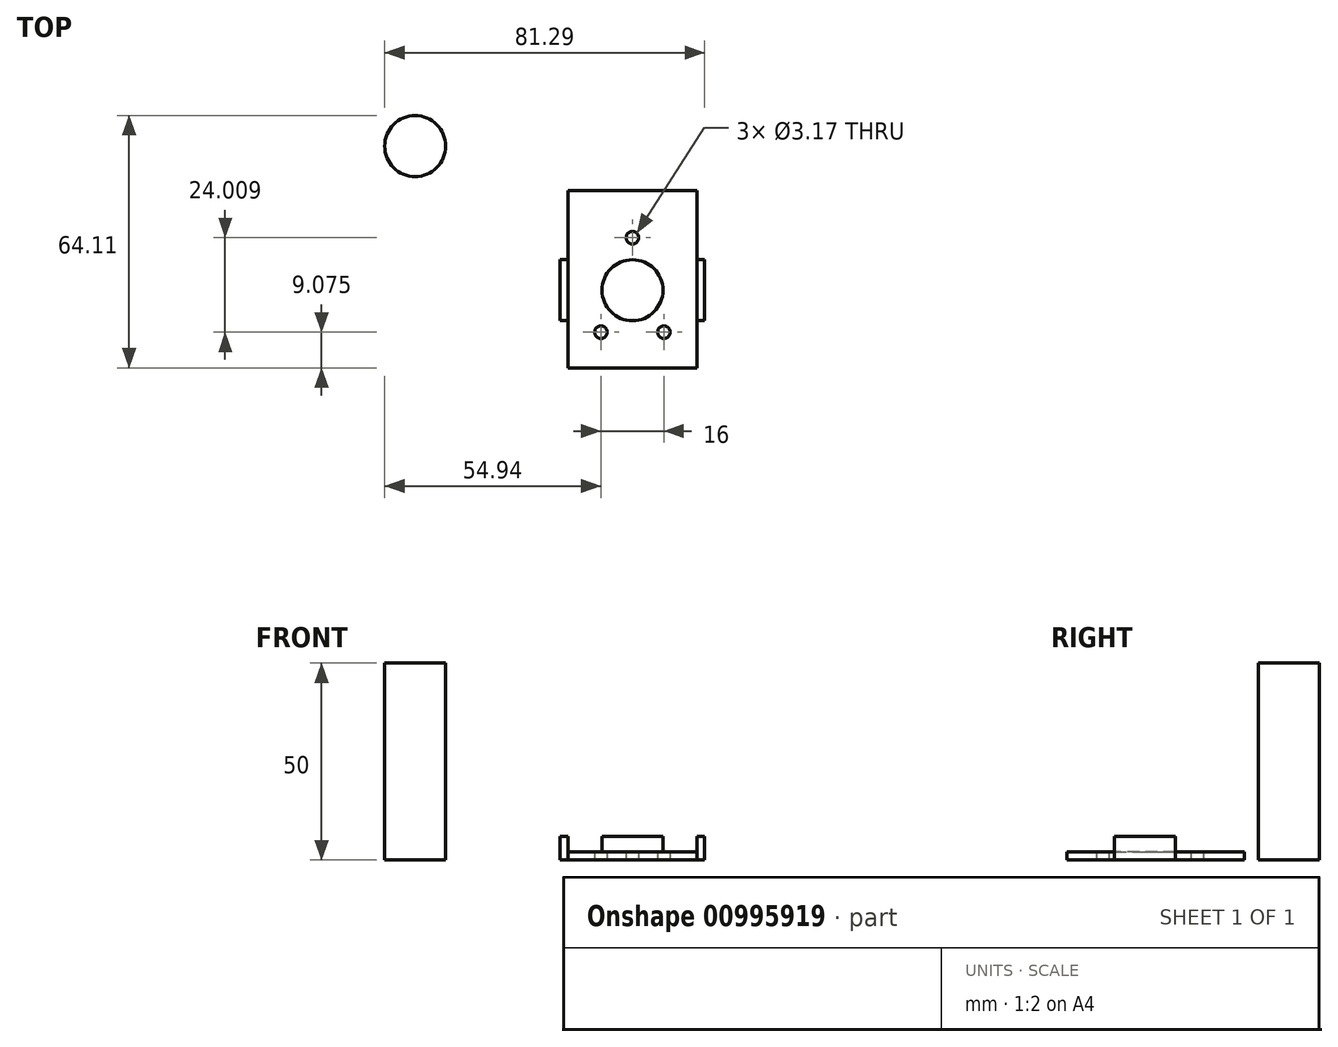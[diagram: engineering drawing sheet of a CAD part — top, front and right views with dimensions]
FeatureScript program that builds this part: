
annotation { "Feature Type Name" : "Feature", "Feature Type Description" : "" }
export const myFeature = defineFeature(function(context is Context, id is Id, definition is map)
    precondition{}
    {
        {
            var Q0;
            Q0=qCreatedBy(makeId("Top.planeOp"),FACE);
            var sketch = newSketch(context, id + "F0", { "sketchPlane" : qUnion([Q0])});
            skCircle(sketch, "E0", {"center": v(0, 0) * mm, "radius": 7.75 * mm});
            skSolve(sketch);
        }
        {
            var Q0;
            Q0 = qSketchRegion(id + "F0", true);
            extrude(context, id + "F1", {"entities" : qUnion([Q0]), "depth" : 50 * mm, "offsetDistance" : 25 * mm});
        }
        {
            var Q0;
            Q0=qCreatedBy(makeId("Top.planeOp"),FACE);
            var sketch = newSketch(context, id + "F2", { "sketchPlane" : qUnion([Q0])});
            skCircle(sketch, "E1", {"center": v(55.2, -36.61) * mm, "radius": 7.75 * mm});
            skLineSegment(sketch, "E2.bottom", {"start": v(38.84, -11.36) * mm, "end": v(71.54, -11.36) * mm});
            skLineSegment(sketch, "E2.top", {"start": v(38.84, -56.36) * mm, "end": v(71.54, -56.36) * mm});
            skLineSegment(sketch, "E2.left", {"start": v(38.84, -11.36) * mm, "end": v(38.84, -56.36) * mm});
            skLineSegment(sketch, "E2.right", {"start": v(71.54, -11.36) * mm, "end": v(71.54, -56.36) * mm});
            skPoint(sketch, "E3", {"position": v(55.2, -56.36) * mm});
            skCircle(sketch, "E4", {"center": v(47.2, -47.28) * mm, "radius": 1.59 * mm});
            skCircle(sketch, "E5", {"center": v(63.2, -47.28) * mm, "radius": 1.59 * mm});
            skCircle(sketch, "E6", {"center": v(55.2, -23.28) * mm, "radius": 1.59 * mm});
            skPoint(sketch, "E6.centerSnap0", {"position": v(55.2, -11.36) * mm});
            skLineSegment(sketch, "E7", {"start": v(47.2, -47.28) * mm, "end": v(55.2, -36.61) * mm, "construction": true});
            skLineSegment(sketch, "E8", {"start": v(63.2, -47.28) * mm, "end": v(55.2, -36.61) * mm, "construction": true});
            skLineSegment(sketch, "E9", {"start": v(55.2, -36.61) * mm, "end": v(55.2, -23.28) * mm, "construction": true});
            skLineSegment(sketch, "E10.bottom", {"start": v(71.54, -28.86) * mm, "end": v(73.54, -28.86) * mm});
            skLineSegment(sketch, "E10.top", {"start": v(71.54, -44.36) * mm, "end": v(73.54, -44.36) * mm});
            skLineSegment(sketch, "E10.left", {"start": v(71.54, -28.86) * mm, "end": v(71.54, -44.36) * mm});
            skLineSegment(sketch, "E10.right", {"start": v(73.54, -28.86) * mm, "end": v(73.54, -44.36) * mm});
            skLineSegment(sketch, "E11.bottom", {"start": v(38.84, -28.86) * mm, "end": v(36.84, -28.86) * mm});
            skLineSegment(sketch, "E11.top", {"start": v(38.84, -44.36) * mm, "end": v(36.84, -44.36) * mm});
            skLineSegment(sketch, "E11.left", {"start": v(38.84, -28.86) * mm, "end": v(38.84, -44.36) * mm});
            skLineSegment(sketch, "E11.right", {"start": v(36.84, -28.86) * mm, "end": v(36.84, -44.36) * mm});
            skSolve(sketch);
        }
        {
            var Q0;
            {var subQ0=sQuery(id+"F2.wireOp",EDGE,"E10.bottom");var subQ6=sQuery(id+"F2.wireOp",EDGE,"E11.bottom");Q0=qUnion([makeQuery(id+"F2.imprint","IMPRINT",FACE,{"disambiguationData":[TD([[makeQuery(id+"F2.imprint","IMPRINT",EDGE,{"derivedFrom":sQuery(id+"F2.wireOp",EDGE,"E1")}),-1.0]])]}),makeQuery(id+"F2.imprint","IMPRINT",FACE,{"disambiguationData":[TD([[makeQuery(id+"F2.imprint","IMPRINT",EDGE,{"derivedFrom":subQ6}),1.0]])]}),makeQuery(id+"F2.imprint","IMPRINT",FACE,{"disambiguationData":[TD([[makeQuery(id+"F2.imprint","IMPRINT",EDGE,{"derivedFrom":subQ0}),-1.0]])]})]);}
            extrude(context, id + "F3", {"entities" : qUnion([Q0]), "depth" : 2 * mm, "offsetDistance" : 25 * mm});
        }
        {
            var Q0;
            Q0=makeQuery(id+"F2.imprint","IMPRINT",FACE,{"disambiguationData":[TD([[makeQuery(id+"F2.imprint","IMPRINT",EDGE,{"derivedFrom":sQuery(id+"F2.wireOp",EDGE,"E1")}),1.0]])]});
            var Q1;
            {var subQ0=sQuery(id+"F2.wireOp",EDGE,"E11.bottom");Q1=makeQuery(id+"F2.imprint","IMPRINT",FACE,{"disambiguationData":[TD([[makeQuery(id+"F2.imprint","IMPRINT",EDGE,{"derivedFrom":subQ0}),1.0]])]});}
            var Q2;
            {var subQ0=sQuery(id+"F2.wireOp",EDGE,"E10.bottom");Q2=makeQuery(id+"F2.imprint","IMPRINT",FACE,{"disambiguationData":[TD([[makeQuery(id+"F2.imprint","IMPRINT",EDGE,{"derivedFrom":subQ0}),-1.0]])]});}
            extrude(context, id + "F4", {"entities" : qUnion([Q0, Q1, Q2]), "operationType" : NewBodyOperationType.ADD, "depth" : 6 * mm, "offsetDistance" : 25 * mm});
        }
    });
